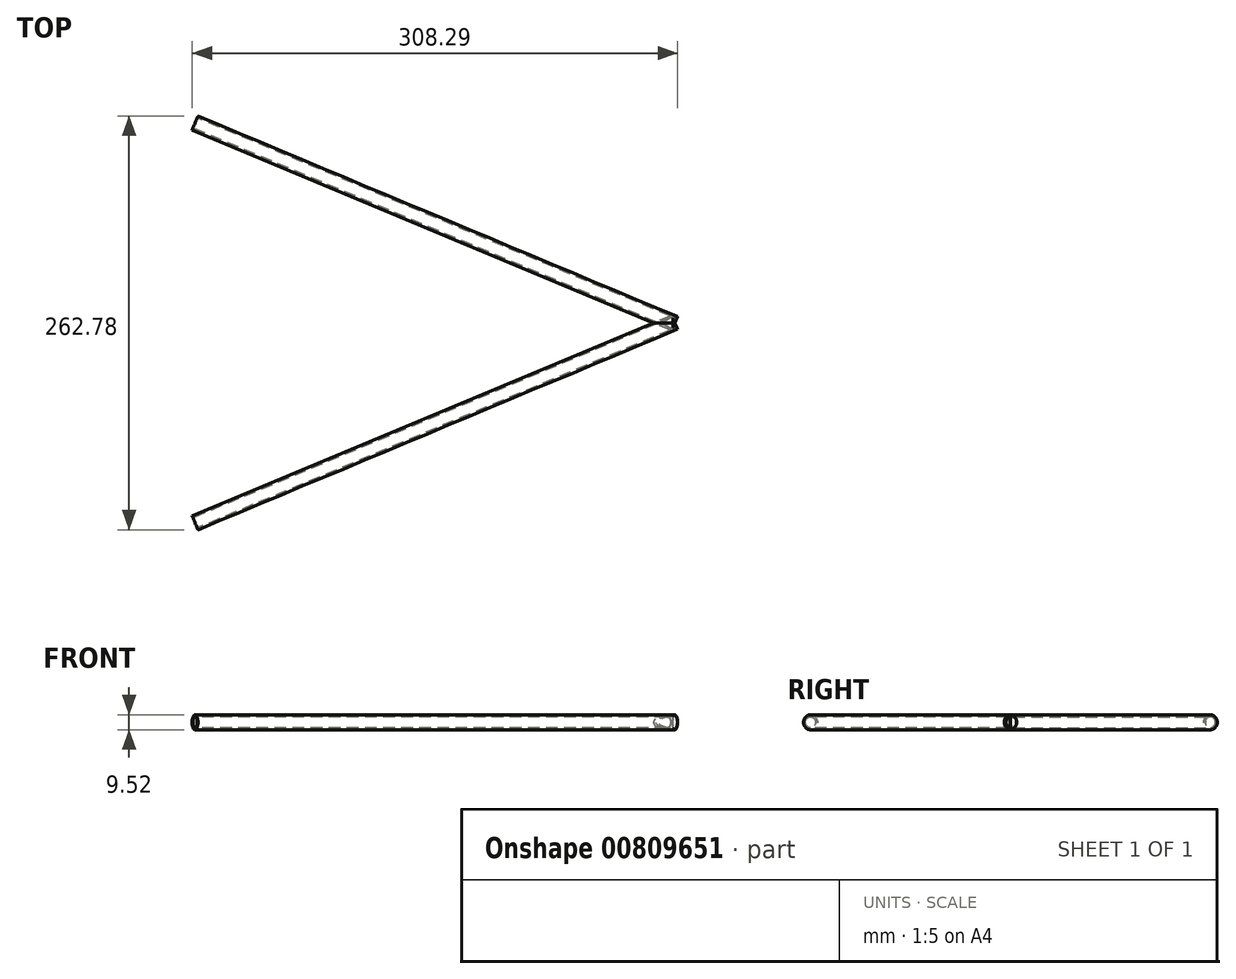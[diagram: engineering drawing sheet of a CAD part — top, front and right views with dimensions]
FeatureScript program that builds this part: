
annotation { "Feature Type Name" : "Feature", "Feature Type Description" : "" }
export const myFeature = defineFeature(function(context is Context, id is Id, definition is map)
    precondition{}
    {
        {
            var Q0;
            Q0=qCreatedBy(makeId("Right.planeOp"),FACE);
            var sketch = newSketch(context, id + "F0", { "sketchPlane" : qUnion([Q0])});
            skPoint(sketch, "E0", {"position": v(-127, 0) * mm});
            skPoint(sketch, "E1", {"position": v(-127, 43.64) * mm});
            skSolve(sketch);
        }
        {
            var Q0;
            Q0=qCreatedBy(makeId("Right.planeOp"),FACE);
            cPlane(context, id + "F1", {"entities" : qUnion([Q0]), "cplaneType" : CPlaneType.OFFSET, "offset" : 25.4 * mm, "width" : 152.4 * mm, "height" : 152.4 * mm});
        }
        {
            var Q0;
            Q0=qCreatedBy(id+"F1.planeOp",FACE);
            var sketch = newSketch(context, id + "F2", { "sketchPlane" : qUnion([Q0])});
            skPoint(sketch, "E2", {"position": v(-187.7, 0) * mm});
            skSolve(sketch);
        }
        {
            var Q0;
            Q0=sQuery(id+"F2.wireOp",VERTEX,"E2");
            var Q1;
            Q1=sQuery(id+"F0.wireOp",VERTEX,"E0");
            var Q2;
            Q2=sQuery(id+"F0.wireOp",VERTEX,"E1");
            cPlane(context, id + "F3", {"entities" : qUnion([Q0, Q1, Q2]), "cplaneType" : CPlaneType.THREE_POINT, "offset" : 25.4 * mm, "width" : 152.4 * mm, "height" : 152.4 * mm});
        }
        {
            var Q0;
            Q0=qCreatedBy(id+"F3.planeOp",FACE);
            var sketch = newSketch(context, id + "F4", { "sketchPlane" : qUnion([Q0])});
            skCircle(sketch, "E3", {"center": v(117.16, 0) * mm, "radius": 4.76 * mm});
            skCircle(sketch, "E4", {"center": v(117.16, 0) * mm, "radius": 3.52 * mm});
            skSolve(sketch);
        }
        {
            var Q0;
            Q0=makeQuery(id+"F4.imprint","IMPRINT",FACE,{"disambiguationData":[TD([[makeQuery(id+"F4.imprint","IMPRINT",EDGE,{"derivedFrom":sQuery(id+"F4.wireOp",EDGE,"E3")}),1.0]])]});
            extrude(context, id + "F5", {"entities" : qUnion([Q0]), "oppositeDirection" : true, "depth" : 330.2 * mm, "offsetDistance" : 25.4 * mm});
        }
        {
            var Q0;
            Q0=makeQuery(id+"F5.opExtrude","SWEPT_BODY",BODY,{"disambiguationData":[OSD([sQuery(id+"F4.wireOp",EDGE,"E3"),sQuery(id+"F4.wireOp",EDGE,"E4")])]});
            var Q1;
            Q1=qCreatedBy(makeId("Front.planeOp"),FACE);
            mirror(context, id + "F6", {"operationType" : NewBodyOperationType.ADD, "entities" : qUnion([Q0]), "mirrorPlane" : qUnion([Q1])});
        }
    });
